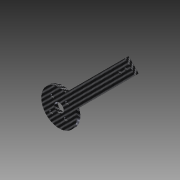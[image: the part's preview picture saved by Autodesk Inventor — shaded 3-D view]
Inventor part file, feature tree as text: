
AUTODESK INVENTOR PART (.ipt)
format: ipt  version: 2015 (Build 190159000, 159)  size: 102,400 bytes
history: native  units: mm
features: extrude x2, sketch x2
ambient origin geometry x8: Origin, YZ Plane, XZ Plane, XY Plane, X Axis, Y Axis, Z Axis, Center Point
bodies: Solid1 (feature_tree)
feature tree (4):
  extrude  "Extrusion1"  Depth=3.0mm
  extrude  "Extrusion2"  Depth=3.0mm
  sketch  "Sketch1"  dims[d3=3.0mm d4=3.0mm]
  sketch  "Sketch2"  dims[d5=3.0mm d6=3.0mm d7=3.0mm d8=0.0mm d9=8.0mm d10=3.0mm d11=0.0mm]
